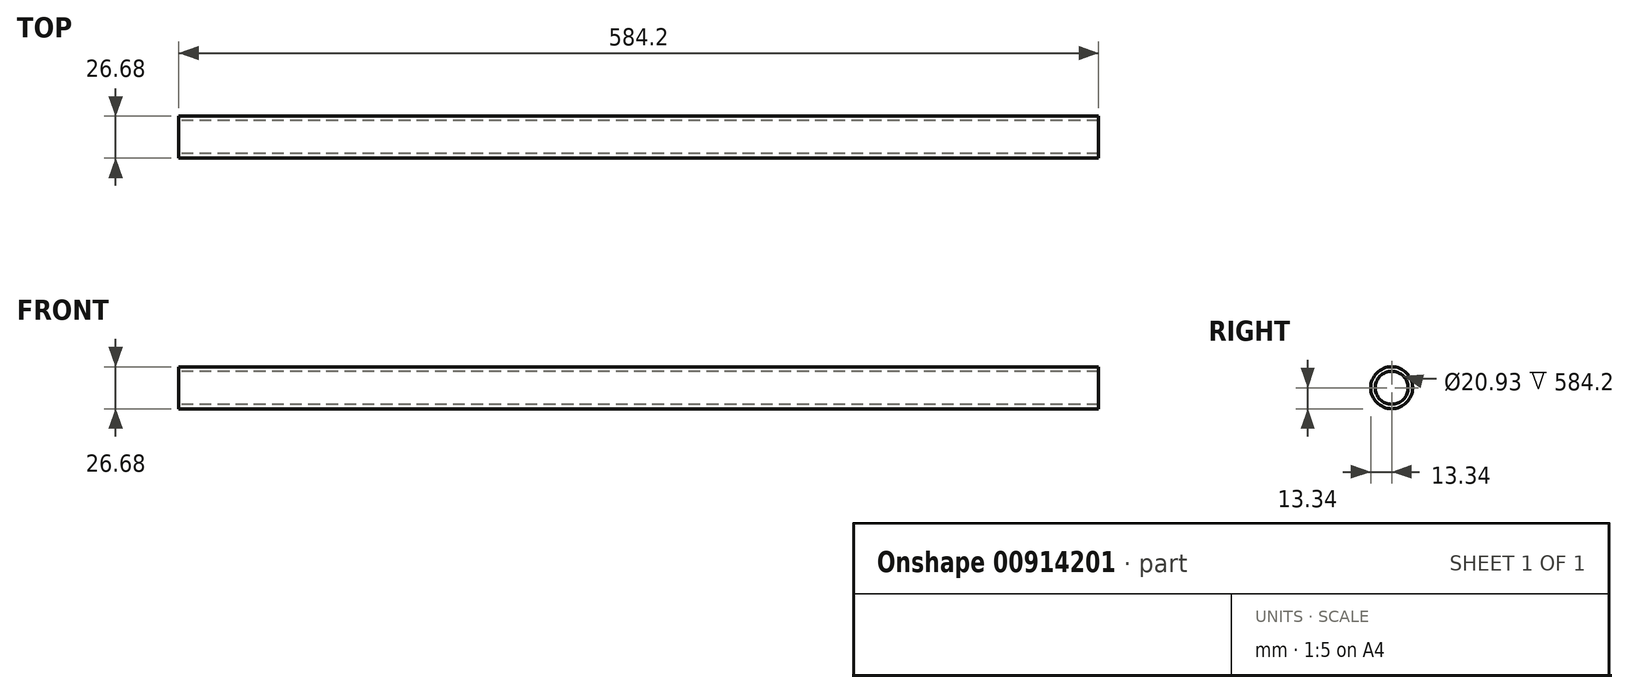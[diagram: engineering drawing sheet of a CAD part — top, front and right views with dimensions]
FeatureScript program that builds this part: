
annotation { "Feature Type Name" : "Feature", "Feature Type Description" : "" }
export const myFeature = defineFeature(function(context is Context, id is Id, definition is map)
    precondition{}
    {
        {
            var Q0;
            Q0=qCreatedBy(makeId("Right.planeOp"),FACE);
            var sketch = newSketch(context, id + "F0", { "sketchPlane" : qUnion([Q0])});
            skCircle(sketch, "E0", {"center": v(0, 0) * mm, "radius": 13.34 * mm});
            skCircle(sketch, "E1", {"center": v(0, 0) * mm, "radius": 10.46 * mm});
            skSolve(sketch);
        }
        {
            var Q0;
            Q0=qSketchRegion(id+"F0",true);
            extrude(context, id + "F1", {"entities" : qUnion([Q0]), "depth" : 584.2 * mm, "offsetDistance" : 25.4 * mm});
        }
    });
